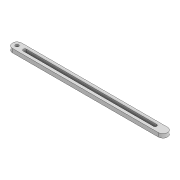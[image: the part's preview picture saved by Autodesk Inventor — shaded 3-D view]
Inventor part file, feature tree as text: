
AUTODESK INVENTOR PART (.ipt)
format: ipt  version: 2022 (Build 260153000, 153)  size: 91,136 bytes
history: native  units: mm
features: extrude x1, sketch x1
ambient origin geometry x8: Origin, YZ Plane, XZ Plane, XY Plane, X Axis, Y Axis, Z Axis, Center Point
bodies: Solid1 (feature_tree)
feature tree (2):
  extrude  "Extrusion1"  Depth=12.0mm
  sketch  "Sketch1"  dims[d0=188.328mm d1=12.0mm d2=4.2mm d3=4.2mm d4=5.0mm d5=0.0mm d6=10.0mm d7=10.0mm]
